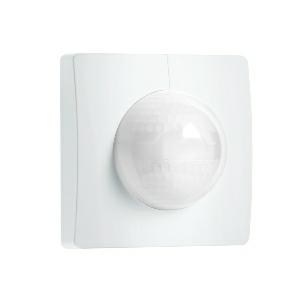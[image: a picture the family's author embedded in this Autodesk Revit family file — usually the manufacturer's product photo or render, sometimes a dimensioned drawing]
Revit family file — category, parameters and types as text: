
# Revit family: is_3180_055769
name_source: partatom
category: Elektroinstallationen
revit_build: Autodesk Revit 2016 (Build: 20190508_0715(x64)
units: mm (PartAtom-declared; Revit-internal decimal feet)

## family parameters
Basisbauteil = Fläche
Beim Laden mit Abzugskörper schneiden = Nein
Bemaßung runder Anschluss = Durchmesser verwenden
Beschriftungsausrichtung beibehalten = Nein
Gemeinsam genutzt = Nein
Raumberechnungspunkt = Nein
Teiletyp = Normal

## types (1)
- IS 3180
    Apparent Load = 0 VA
    Beschreibung = Type: Motion detectors; Dimensions (L x W x H): 78 x 94 x 94 mm; Mains power supply: 220 – 240 V / 50 – 60 Hz; Power consumption: 0,3 W; Sensor Technology: passive infrared; Application, place: Indoors; Application, room: corridor / aisle, function room / ancillary room, stairwell, multi-storey / underground car park, outdoors, all round the building, courtyard & driveway, Indoors; Installation site: wall, corner; Installation: Concealed wiring; Switching zones: 448 switching zones; Electronic scalability: No; Mechanical scalability: No; Mounting height: 1,80 – 2,50 m; Optimum mounting height: 2 m; Detection angle: 180 °; Angle of aperture: 90 °; Sneak-by guard: Yes; Capability of masking out individual segments: Yes; Reach, radial: r = 3 m (14 m²) / r = 4 m (25 m²); Reach, tangential: r = 6 m (57 m²) / r = 20 m (628 m²); Twilight setting TEACH: Yes; Twilight setting: 2 – 1000 lx; Time setting: 5 sec – 15 min; Constant-lighting control: No; Basic light level function: No; Functions: Normal / test mode, Manual ON / ON-OFF; Settings via: Remote control, Potentiometers, Smart Remote; With remote control: No; Interconnection: Yes; Type of interconnection: Master/master; IP-rating: IP20; Material: Plastic; Ambient temperature: -20 – 50 °C; Colour: white; Colour, RAL: 9003; Manufacturer's Warranty: 5 years; Version: PF - concealed, sq.; PU1, EAN: 4007841055769
    Height = 94 mm  [stored 0.308399 ft]
    Hersteller = Steinel
    Length = 78 mm  [stored 0.255906 ft]
    Maximum range = 22.153 m
    ModVariant = Nein
    Modell = 055769
    Mounting Type = Recessed
    Number of Poles = 1
    OnlyDefault = Ja
    Power Factor = 1
    Product Name = IS 3180
    Product group = Sensor-switched indoor light
    ProductGroupID = 30
    Protection Class = Protection class
    Protection Degree = IP 20
    RlxData = <blob elided: 167989 chars, md5=c6ed07b2>
    Sensor characteristics = Semi circular 145°-300°
    Sensor type = Passive (infrared)
    SensorDataFile = <blob elided: 5082 chars, md5=d953030a>
    Type of entry = Motion
    Typenbild = produkt1_055769.jpg
    Typenkommentare = Product without accessories
    URL = http://relux.com
    VarID = ---
    Voltage = 0 V
    Vorgabe-Ansicht = 1800 mm
    Weight = 0.00 kg
    Width = 94 mm  [stored 0.308399 ft]

note: [stored X ft] marks values corroborated as IEEE doubles in the binary element streams (Revit-internal decimal feet)

## geometry (parser evidence)
native form markers: Sweep x21
no freeform markers — native parametric forms only
